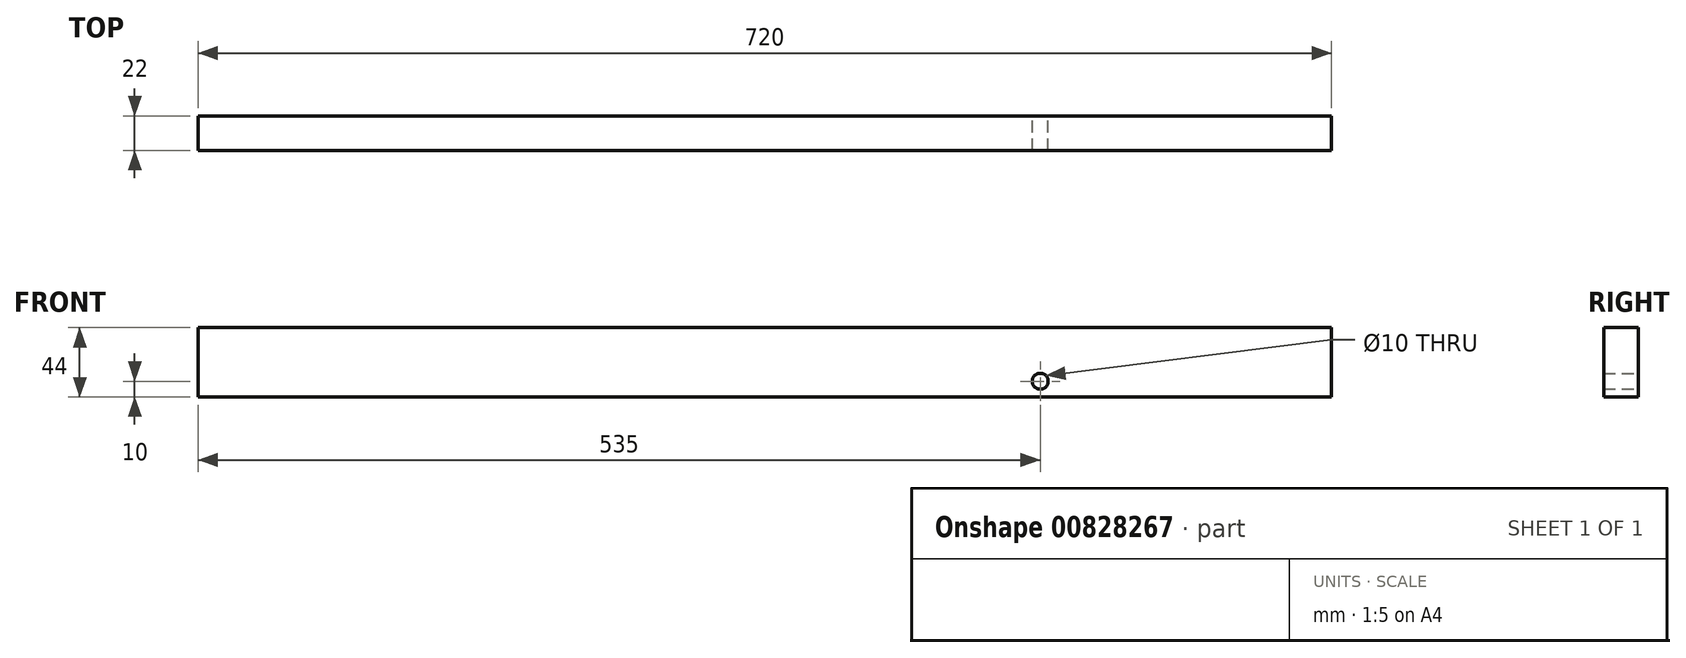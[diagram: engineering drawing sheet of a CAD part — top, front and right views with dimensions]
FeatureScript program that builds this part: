
annotation { "Feature Type Name" : "Feature", "Feature Type Description" : "" }
export const myFeature = defineFeature(function(context is Context, id is Id, definition is map)
    precondition{}
    {
        {
            var Q0;
            Q0=qCreatedBy(makeId("Front.planeOp"),FACE);
            var sketch = newSketch(context, id + "F0", { "sketchPlane" : qUnion([Q0])});
            skLineSegment(sketch, "E0.bottom", {"start": v(-360, 0) * mm, "end": v(360, 0) * mm});
            skLineSegment(sketch, "E0.top", {"start": v(-360, 44) * mm, "end": v(360, 44) * mm});
            skLineSegment(sketch, "E0.left", {"start": v(-360, 0) * mm, "end": v(-360, 44) * mm});
            skLineSegment(sketch, "E0.right", {"start": v(360, 0) * mm, "end": v(360, 44) * mm});
            skPoint(sketch, "E0.middle", {"position": v(0, 22) * mm});
            skCircle(sketch, "E1", {"center": v(175, 10) * mm, "radius": 5 * mm});
            skSolve(sketch);
        }
        {
            var Q0;
            Q0=makeQuery(id+"F0.imprint","IMPRINT",FACE,{"disambiguationData":[TD([[makeQuery(id+"F0.imprint","IMPRINT",EDGE,{"derivedFrom":sQuery(id+"F0.wireOp",EDGE,"E0.bottom")}),1.0]])]});
            extrude(context, id + "F1", {"entities" : qUnion([Q0]), "depth" : 22 * mm, "offsetDistance" : 25 * mm});
        }
    });
